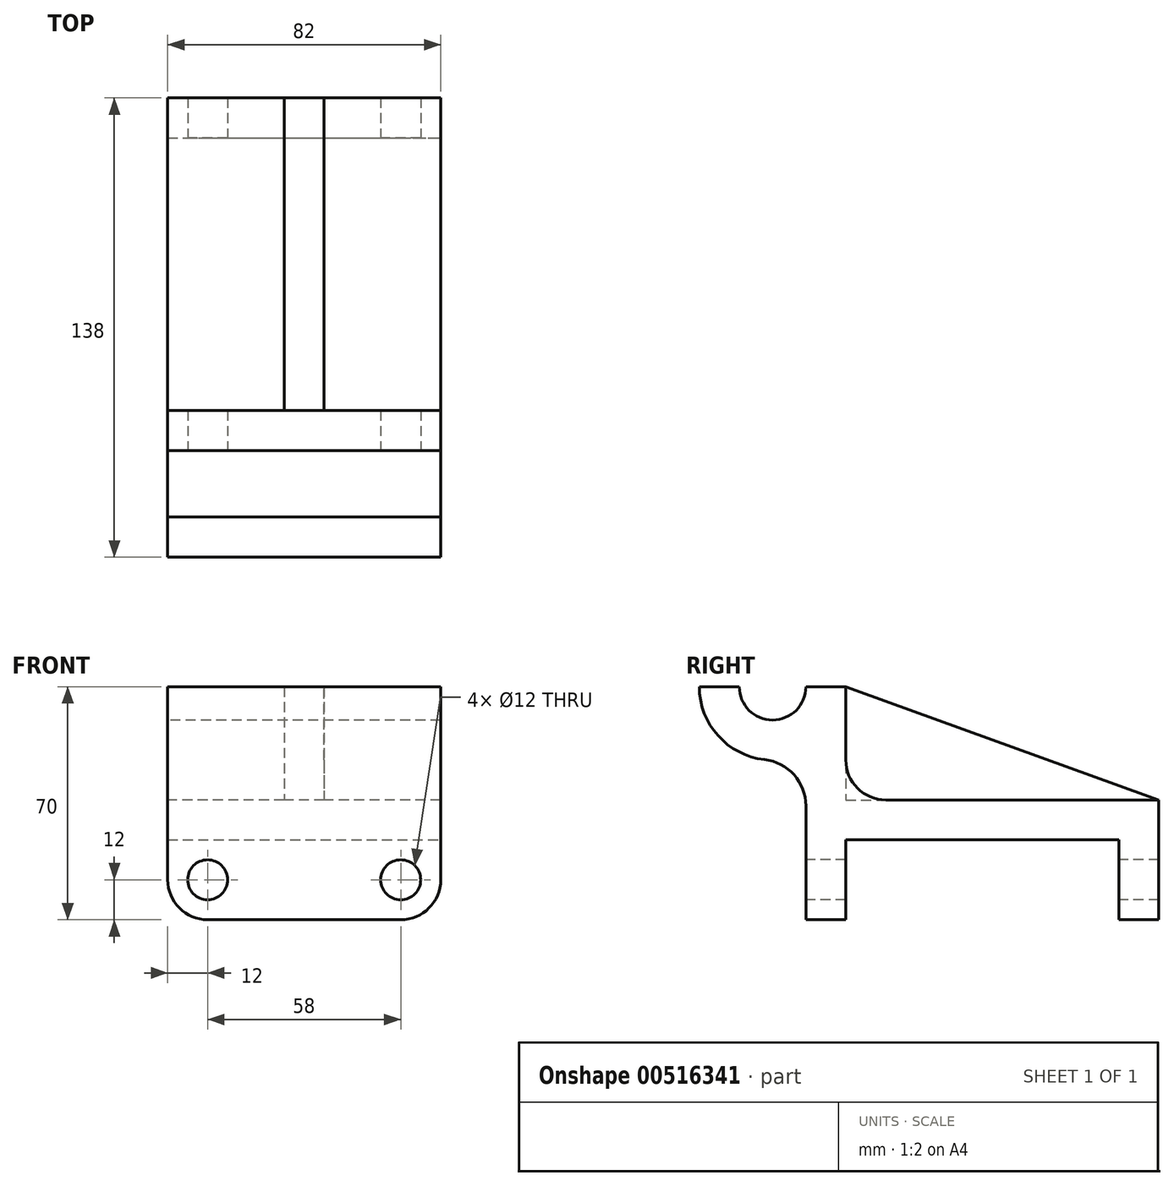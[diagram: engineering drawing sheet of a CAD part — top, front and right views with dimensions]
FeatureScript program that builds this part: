
annotation { "Feature Type Name" : "Feature", "Feature Type Description" : "" }
export const myFeature = defineFeature(function(context is Context, id is Id, definition is map)
    precondition{}
    {
        {
            var Q0;
            Q0=qCreatedBy(makeId("Top.planeOp"),FACE);
            var sketch = newSketch(context, id + "F0", { "sketchPlane" : qUnion([Q0])});
            skLineSegment(sketch, "E0.bottom", {"start": v(41, 53) * mm, "end": v(-41, 53) * mm});
            skLineSegment(sketch, "E0.top", {"start": v(41, -53) * mm, "end": v(-41, -53) * mm});
            skLineSegment(sketch, "E0.left", {"start": v(41, 53) * mm, "end": v(41, -53) * mm});
            skLineSegment(sketch, "E0.right", {"start": v(-41, 53) * mm, "end": v(-41, -53) * mm});
            skPoint(sketch, "E0.middle", {"position": v(0, 0) * mm});
            skSolve(sketch);
        }
        {
            var Q0;
            Q0 = qSketchRegion(id + "F0", true);
            extrude(context, id + "F1", {"entities" : qUnion([Q0]), "depth" : 36 * mm, "offsetDistance" : 25 * mm});
        }
        {
            var Q0;
            Q0=makeQuery(id+"F1.opExtrude","SWEPT_FACE",FACE,{"disambiguationData":[OSD([sQuery(id+"F0.wireOp",EDGE,"E0.top")])]});
            var sketch = newSketch(context, id + "F2", { "sketchPlane" : qUnion([Q0])});
            skLineSegment(sketch, "E1", {"start": v(41, 0) * mm, "end": v(29, 0) * mm});
            skLineSegment(sketch, "E2", {"start": v(29, 0) * mm, "end": v(-41, 0) * mm});
            skLineSegment(sketch, "E3", {"start": v(-41, 0) * mm, "end": v(-29, 0) * mm});
            skLineSegment(sketch, "E4", {"start": v(-29, 0) * mm, "end": v(-29, 19.34) * mm});
            skLineSegment(sketch, "E5", {"start": v(26.79, 0) * mm, "end": v(29, 0) * mm});
            skLineSegment(sketch, "E6", {"start": v(29, 0) * mm, "end": v(29, 18.35) * mm});
            skLineSegment(sketch, "E7", {"start": v(29, 0) * mm, "end": v(29, 12) * mm});
            skCircle(sketch, "E8", {"center": v(29, 12) * mm, "radius": 6 * mm});
            skLineSegment(sketch, "E9", {"start": v(-29, 0) * mm, "end": v(-29, 12) * mm});
            skCircle(sketch, "E10", {"center": v(-29, 12) * mm, "radius": 6 * mm});
            skSolve(sketch);
        }
        {
            var Q0;
            Q0=makeQuery(id+"F1.opExtrude","CAP_EDGE",EDGE,{"disambiguationData":[OSD([sQuery(id+"F0.wireOp",EDGE,"E0.right")])],"isStart":true});
            fillet(context, id + "F3", {"entities" : qUnion([Q0]), "radius" : 12 * mm, "tangentPropagation" : true, "allowEdgeOverflow" : false});
        }
        {
            var Q0;
            {var subQ0=sQuery(id+"F2.wireOp",EDGE,"E9");var subQ1=sQuery(id+"F2.wireOp",EDGE,"E4");var subQ2=makeQuery(id+"F2.imprint","INTERSECT",VERTEX,{"derivedFrom":[subQ1,subQ0]});Q0=makeQuery(id+"F2.imprint","IMPRINT",FACE,{"disambiguationData":[TD([[makeQuery(id+"F2.imprint","IMPRINT",EDGE,{"disambiguationData":[TD([[subQ2,-1.0]])],"derivedFrom":subQ1}),1.0]])]});}
            var Q1;
            {var subQ0=sQuery(id+"F2.wireOp",EDGE,"E9");var subQ1=sQuery(id+"F2.wireOp",EDGE,"E4");var subQ2=makeQuery(id+"F2.imprint","INTERSECT",VERTEX,{"derivedFrom":[subQ1,subQ0]});Q1=makeQuery(id+"F2.imprint","IMPRINT",FACE,{"disambiguationData":[TD([[makeQuery(id+"F2.imprint","IMPRINT",EDGE,{"disambiguationData":[TD([[subQ2,-1.0]])],"derivedFrom":subQ1}),-1.0]])]});}
            var Q2;
            {var subQ0=sQuery(id+"F2.wireOp",EDGE,"E7");var subQ1=sQuery(id+"F2.wireOp",EDGE,"E6");var subQ2=makeQuery(id+"F2.imprint","INTERSECT",VERTEX,{"derivedFrom":[subQ1,subQ0]});Q2=makeQuery(id+"F2.imprint","IMPRINT",FACE,{"disambiguationData":[TD([[makeQuery(id+"F2.imprint","IMPRINT",EDGE,{"disambiguationData":[TD([[subQ2,-1.0]])],"derivedFrom":subQ1}),-1.0]])]});}
            var Q3;
            {var subQ0=sQuery(id+"F2.wireOp",EDGE,"E7");var subQ1=sQuery(id+"F2.wireOp",EDGE,"E6");var subQ2=makeQuery(id+"F2.imprint","INTERSECT",VERTEX,{"derivedFrom":[subQ1,subQ0]});Q3=makeQuery(id+"F2.imprint","IMPRINT",FACE,{"disambiguationData":[TD([[makeQuery(id+"F2.imprint","IMPRINT",EDGE,{"disambiguationData":[TD([[subQ2,-1.0]])],"derivedFrom":subQ1}),1.0]])]});}
            extrude(context, id + "F4", {"entities" : qUnion([Q0, Q1, Q2, Q3]), "operationType" : NewBodyOperationType.REMOVE, "oppositeDirection" : true, "depth" : 191.1 * mm, "offsetDistance" : 25 * mm});
        }
        {
            var Q0;
            Q0=makeQuery(id+"F1.opExtrude","CAP_EDGE",EDGE,{"disambiguationData":[OSD([sQuery(id+"F0.wireOp",EDGE,"E0.left")])],"isStart":true});
            fillet(context, id + "F5", {"entities" : qUnion([Q0]), "radius" : 12 * mm, "tangentPropagation" : true, "allowEdgeOverflow" : false});
        }
        {
            var Q0;
            Q0=makeQuery(id+"F1.opExtrude","SWEPT_FACE",FACE,{"disambiguationData":[OSD([sQuery(id+"F0.wireOp",EDGE,"E0.left")])]});
            var sketch = newSketch(context, id + "F6", { "sketchPlane" : qUnion([Q0])});
            skLineSegment(sketch, "E11", {"start": v(-30.1, 36) * mm, "end": v(-30.1, 24) * mm});
            skLineSegment(sketch, "E12", {"start": v(-53, 12) * mm, "end": v(-41, 12) * mm});
            skLineSegment(sketch, "E13", {"start": v(-41, 12) * mm, "end": v(-41, 24) * mm});
            skLineSegment(sketch, "E14", {"start": v(-41, 24) * mm, "end": v(-30.1, 24) * mm});
            skLineSegment(sketch, "E15", {"start": v(53, 12) * mm, "end": v(41, 12) * mm});
            skLineSegment(sketch, "E16", {"start": v(-30.1, 24) * mm, "end": v(41, 24) * mm});
            skLineSegment(sketch, "E17", {"start": v(41, 24) * mm, "end": v(41, 12) * mm});
            skLineSegment(sketch, "E18", {"start": v(-41, 12) * mm, "end": v(-41, 0) * mm});
            skLineSegment(sketch, "E19", {"start": v(41, 12) * mm, "end": v(41, -1.92) * mm});
            skSolve(sketch);
        }
        {
            var Q0;
            {var subQ1=sQuery(id+"F6.wireOp",EDGE,"E13");Q0=makeQuery(id+"F6.imprint","IMPRINT",FACE,{"disambiguationData":[TD([[makeQuery(id+"F6.imprint","IMPRINT",EDGE,{"derivedFrom":subQ1}),-1.0]])]});}
            extrude(context, id + "F7", {"entities" : qUnion([Q0]), "operationType" : NewBodyOperationType.REMOVE, "oppositeDirection" : true, "depth" : 174.6 * mm, "offsetDistance" : 25 * mm});
        }
        {
            var Q0;
            Q0=makeQuery(id+"F7.boolean.opBoolean","COPY",FACE,{"disambiguationData":[TD([makeQuery(id+"F4.boolean.opBoolean","COPY",FACE,{"derivedFrom":makeQuery(id+"F4.opExtrude","SWEPT_FACE",FACE,{"disambiguationData":[OSD([sQuery(id+"F2.wireOp",EDGE,"E8")])]})}),makeQuery(id+"F4.boolean.opBoolean","COPY",FACE,{"derivedFrom":makeQuery(id+"F4.opExtrude","SWEPT_FACE",FACE,{"disambiguationData":[OSD([sQuery(id+"F2.wireOp",EDGE,"E10")])]})}),makeQuery(id+"F7.opExtrude","SWEPT_FACE",FACE,{"disambiguationData":[OSD([sQuery(id+"F6.wireOp",EDGE,"E13")])]}),makeQuery(id+"F7.opExtrude","SWEPT_FACE",FACE,{"disambiguationData":[OSD([sQuery(id+"F6.wireOp",EDGE,"E17")])]})])],"derivedFrom":makeQuery(id+"F7.opExtrude","SWEPT_FACE",FACE,{"disambiguationData":[OSD([sQuery(id+"F0.wireOp",EDGE,"E0.left")])]})});
            extrude(context, id + "F8", {"entities" : qUnion([Q0]), "operationType" : NewBodyOperationType.REMOVE, "oppositeDirection" : true, "depth" : 24 * mm, "offsetDistance" : 25 * mm});
        }
        {
            var Q0;
            {var subQ0=sQuery(id+"F6.wireOp",EDGE,"E11");Q0=makeQuery(id+"F6.imprint","IMPRINT",FACE,{"disambiguationData":[TD([[makeQuery(id+"F6.imprint","IMPRINT",EDGE,{"derivedFrom":subQ0}),-1.0]])]});}
            var sketch = newSketch(context, id + "F9", { "sketchPlane" : qUnion([Q0])});
            skLineSegment(sketch, "E20.0", {"start": v(-41, 12) * mm, "end": v(-41, 24) * mm});
            skLineSegment(sketch, "E21", {"start": v(-41, 12) * mm, "end": v(-41, -6.95) * mm});
            skLineSegment(sketch, "E22.0", {"start": v(41, 24) * mm, "end": v(41, 12) * mm});
            skLineSegment(sketch, "E23", {"start": v(41, 12) * mm, "end": v(41, -13.93) * mm});
            skLineSegment(sketch, "E24.bottom", {"start": v(-41, 12) * mm, "end": v(41, 12) * mm});
            skLineSegment(sketch, "E24.top", {"start": v(-41, -0.96) * mm, "end": v(41, -0.96) * mm});
            skLineSegment(sketch, "E24.left", {"start": v(-41, 12) * mm, "end": v(-41, -0.96) * mm});
            skLineSegment(sketch, "E24.right", {"start": v(41, 12) * mm, "end": v(41, -0.96) * mm});
            skSolve(sketch);
        }
        {
            var Q0;
            Q0=makeQuery(id+"F9.imprint","IMPRINT",FACE,{"disambiguationData":[TD([[makeQuery(id+"F9.imprint","IMPRINT",EDGE,{"derivedFrom":sQuery(id+"F9.wireOp",EDGE,"E24.bottom")}),-1.0]])]});
            extrude(context, id + "F10", {"entities" : qUnion([Q0]), "operationType" : NewBodyOperationType.REMOVE, "oppositeDirection" : true, "depth" : 116.9 * mm, "offsetDistance" : 25 * mm});
        }
        {
            var Q0;
            Q0=makeQuery(id+"F1.opExtrude","CAP_FACE",FACE,{"disambiguationData":[OSD([sQuery(id+"F0.wireOp",EDGE,"E0.bottom"),sQuery(id+"F0.wireOp",EDGE,"E0.top"),sQuery(id+"F0.wireOp",EDGE,"E0.left"),sQuery(id+"F0.wireOp",EDGE,"E0.right")])],"isStart":false});
            var sketch = newSketch(context, id + "F11", { "sketchPlane" : qUnion([Q0])});
            skLineSegment(sketch, "E25", {"start": v(-41, 53) * mm, "end": v(41, 53) * mm});
            skLineSegment(sketch, "E26", {"start": v(41, 53) * mm, "end": v(0, 53) * mm});
            skLineSegment(sketch, "E27", {"start": v(0, 53) * mm, "end": v(-6, 53) * mm});
            skLineSegment(sketch, "E28", {"start": v(-6, 53) * mm, "end": v(6, 53) * mm});
            skLineSegment(sketch, "E29", {"start": v(6, 53) * mm, "end": v(6, -53) * mm});
            skLineSegment(sketch, "E30", {"start": v(6, -53) * mm, "end": v(-6, -53) * mm});
            skLineSegment(sketch, "E31", {"start": v(-6, -53) * mm, "end": v(-6, 53) * mm});
            skSolve(sketch);
        }
        {
            var Q0;
            Q0 = qSketchRegion(id + "F11", true);
            extrude(context, id + "F12", {"entities" : qUnion([Q0]), "operationType" : NewBodyOperationType.ADD, "depth" : 34 * mm, "offsetDistance" : 25 * mm});
        }
        {
            var Q0;
            Q0=makeQuery(id+"F12.opExtrude","SWEPT_FACE",FACE,{"disambiguationData":[OSD([sQuery(id+"F11.wireOp",EDGE,"E31")])]});
            var sketch = newSketch(context, id + "F13", { "sketchPlane" : qUnion([Q0])});
            skLineSegment(sketch, "E32.0", {"start": v(41, 12) * mm, "end": v(41, 24) * mm});
            skLineSegment(sketch, "E33", {"start": v(-53, 36) * mm, "end": v(41, 70) * mm});
            skSolve(sketch);
        }
        {
            var Q0;
            {var subQ0=sQuery(id+"F13.wireOp",EDGE,"E33");Q0=makeQuery(id+"F13.imprint","IMPRINT",FACE,{"disambiguationData":[TD([[makeQuery(id+"F13.imprint","IMPRINT",EDGE,{"derivedFrom":subQ0}),1.0]])]});}
            extrude(context, id + "F14", {"entities" : qUnion([Q0]), "operationType" : NewBodyOperationType.REMOVE, "oppositeDirection" : true, "depth" : 25 * mm, "offsetDistance" : 25 * mm});
        }
        {
            var Q0;
            Q0=makeQuery(id+"F12.opExtrude","SWEPT_FACE",FACE,{"disambiguationData":[OSD([sQuery(id+"F11.wireOp",EDGE,"E31")])]});
            var sketch = newSketch(context, id + "F15", { "sketchPlane" : qUnion([Q0])});
            skLineSegment(sketch, "E34", {"start": v(41, 70) * mm, "end": v(41, 36) * mm});
            skSolve(sketch);
        }
        {
            var Q0;
            {var subQ0=sQuery(id+"F15.wireOp",EDGE,"E34");Q0=makeQuery(id+"F15.imprint","IMPRINT",FACE,{"disambiguationData":[TD([[makeQuery(id+"F15.imprint","IMPRINT",EDGE,{"derivedFrom":subQ0}),1.0]])]});}
            extrude(context, id + "F16", {"entities" : qUnion([Q0]), "operationType" : NewBodyOperationType.REMOVE, "oppositeDirection" : true, "depth" : 25 * mm, "offsetDistance" : 25 * mm});
        }
        {
            var Q0;
            {var subQ0=sQuery(id+"F11.wireOp",EDGE,"E31");var subQ1=makeQuery(id+"F12.opExtrude","CAP_EDGE",EDGE,{"disambiguationData":[OSD([subQ0])],"isStart":true});var subQ3=sQuery(id+"F0.wireOp",EDGE,"E0.top");var subQ6=sQuery(id+"F0.wireOp",EDGE,"E0.right");var subQ7=sQuery(id+"F0.wireOp",EDGE,"E0.bottom");var subQ10=sQuery(id+"F0.wireOp",EDGE,"E0.left");var subQ11=makeQuery(id+"F1.opExtrude","CAP_FACE",FACE,{"disambiguationData":[OSD([subQ7,subQ3,subQ10,subQ6])],"isStart":false});Q0=makeQuery(id+"F16.boolean.opBoolean","MERGE",FACE,{"derivedFrom":[makeQuery(id+"F12.boolean.opBoolean","SPLIT",FACE,{"disambiguationData":[TD([makeQuery(id+"F1.opExtrude","SWEPT_FACE",FACE,{"disambiguationData":[OSD([subQ10])]})])],"derivedFrom":subQ11}),makeQuery(id+"F12.boolean.opBoolean","SPLIT",FACE,{"disambiguationData":[TD([makeQuery(id+"F1.opExtrude","SWEPT_FACE",FACE,{"disambiguationData":[OSD([subQ6])]})])],"derivedFrom":subQ11}),makeQuery(id+"F16.opExtrude","SWEPT_FACE",FACE,{"disambiguationData":[OSD([subQ0]),TDD([makeQuery(id+"F15.imprint","IMPRINT",EDGE,{"disambiguationData":[TD([[makeQuery(id+"F15.imprint","INTERSECT",VERTEX,{"derivedFrom":[subQ1,sQuery(id+"F15.wireOp",EDGE,"E34")]}),1.0]])],"derivedFrom":subQ1})])]})]});}
            var sketch = newSketch(context, id + "F17", { "sketchPlane" : qUnion([Q0])});
            skLineSegment(sketch, "E35", {"start": v(41, -41) * mm, "end": v(-41, -41) * mm});
            skSolve(sketch);
        }
        {
            var Q0;
            {var subQ0=sQuery(id+"F17.wireOp",EDGE,"E35");var subQ1=sQuery(id+"F11.wireOp",EDGE,"E29");var subQ2=makeQuery(id+"F17.imprint","INTERSECT",VERTEX,{"derivedFrom":[makeQuery(id+"F12.opExtrude","CAP_EDGE",EDGE,{"disambiguationData":[OSD([subQ1])],"isStart":true}),subQ0]});Q0=makeQuery(id+"F17.imprint","IMPRINT",FACE,{"disambiguationData":[TD([[makeQuery(id+"F17.imprint","IMPRINT",EDGE,{"disambiguationData":[TD([[subQ2,1.0]])],"derivedFrom":subQ0}),1.0]])]});}
            extrude(context, id + "F18", {"entities" : qUnion([Q0]), "operationType" : NewBodyOperationType.ADD, "depth" : 34 * mm, "offsetDistance" : 25 * mm});
        }
        {
            var Q0;
            {var subQ3=sQuery(id+"F17.wireOp",EDGE,"E35");var subQ4=sQuery(id+"F0.wireOp",EDGE,"E0.right");Q0=makeQuery(id+"F18.boolean.opBoolean","SPLIT",EDGE,{"disambiguationData":[TD([makeQuery(id+"F1.opExtrude","SWEPT_FACE",FACE,{"disambiguationData":[OSD([subQ4])]})])],"derivedFrom":makeQuery(id+"F18.opExtrude","CAP_EDGE",EDGE,{"disambiguationData":[OSD([subQ3])],"isStart":true})});}
            var Q1;
            {var subQ3=sQuery(id+"F17.wireOp",EDGE,"E35");var subQ4=sQuery(id+"F0.wireOp",EDGE,"E0.left");Q1=makeQuery(id+"F18.boolean.opBoolean","SPLIT",EDGE,{"disambiguationData":[TD([makeQuery(id+"F1.opExtrude","SWEPT_FACE",FACE,{"disambiguationData":[OSD([subQ4])]})])],"derivedFrom":makeQuery(id+"F18.opExtrude","CAP_EDGE",EDGE,{"disambiguationData":[OSD([subQ3])],"isStart":true})});}
            fillet(context, id + "F19", {"entities" : qUnion([Q0, Q1]), "radius" : 12 * mm, "tangentPropagation" : true, "allowEdgeOverflow" : false});
        }
        {
            var Q0;
            {var subQ0=sQuery(id+"F0.wireOp",EDGE,"E0.right");Q0=makeQuery(id+"F18.boolean.opBoolean","MERGE",FACE,{"derivedFrom":[makeQuery(id+"F1.opExtrude","SWEPT_FACE",FACE,{"disambiguationData":[OSD([subQ0])]}),makeQuery(id+"F18.opExtrude","SWEPT_FACE",FACE,{"disambiguationData":[OSD([subQ0])]})]});}
            var sketch = newSketch(context, id + "F20", { "sketchPlane" : qUnion([Q0])});
            skArc(sketch, "E36", {"start": v(41, 70) * mm, "mid": v(63, 48) * mm, "end": v(85, 70) * mm});
            skCircle(sketch, "E37", {"center": v(63, 70) * mm, "radius": 10 * mm});
            skLineSegment(sketch, "E38", {"start": v(41, 70) * mm, "end": v(85, 70) * mm});
            skSolve(sketch);
        }
        {
            var Q0;
            {var subQ0=sQuery(id+"F20.wireOp",EDGE,"E38");var subQ1=sQuery(id+"F20.wireOp",EDGE,"E36");var subQ2=makeQuery(id+"F20.imprint","INTERSECT",VERTEX,{"derivedFrom":[subQ1,subQ0]});Q0=makeQuery(id+"F20.imprint","IMPRINT",FACE,{"disambiguationData":[TD([[makeQuery(id+"F20.imprint","IMPRINT",EDGE,{"disambiguationData":[TD([[subQ2,1.0]])],"derivedFrom":subQ0}),-1.0]])]});}
            var Q1;
            {var subQ0=sQuery(id+"F20.wireOp",EDGE,"E38");var subQ1=sQuery(id+"F20.wireOp",EDGE,"E36");var subQ2=sQuery(id+"F0.wireOp",EDGE,"E0.right");var subQ3=makeQuery(id+"F20.imprint","INTERSECT",VERTEX,{"derivedFrom":[makeQuery(id+"F18.opExtrude","SWEPT_EDGE",EDGE,{"disambiguationData":[OSD([subQ2,sQuery(id+"F17.wireOp",EDGE,"E35")])]}),subQ1,subQ0]});Q1=makeQuery(id+"F20.imprint","IMPRINT",FACE,{"disambiguationData":[TD([[makeQuery(id+"F20.imprint","IMPRINT",EDGE,{"disambiguationData":[TD([[subQ3,-1.0]])],"derivedFrom":subQ1}),1.0]])]});}
            var Q2;
            {var subQ0=sQuery(id+"F0.wireOp",EDGE,"E0.left");Q2=makeQuery(id+"F18.boolean.opBoolean","MERGE",FACE,{"derivedFrom":[makeQuery(id+"F1.opExtrude","SWEPT_FACE",FACE,{"disambiguationData":[OSD([subQ0])]}),makeQuery(id+"F18.opExtrude","SWEPT_FACE",FACE,{"disambiguationData":[OSD([subQ0])]})]});}
            extrude(context, id + "F21", {"entities" : qUnion([Q0, Q1]), "operationType" : NewBodyOperationType.ADD, "endBound" : BoundingType.UP_TO_SURFACE, "oppositeDirection" : true, "depth" : 86 * mm, "endBoundEntityFace" : qUnion([Q2]), "offsetDistance" : 25 * mm});
        }
        {
            var Q0;
            {var subQ0=sQuery(id+"F11.wireOp",EDGE,"E30");var subQ1=sQuery(id+"F0.wireOp",EDGE,"E0.top");Q0=makeQuery(id+"F21.boolean.opBoolean","INTERSECT",EDGE,{"derivedFrom":[makeQuery(id+"F18.boolean.opBoolean","MERGE",FACE,{"derivedFrom":[makeQuery(id+"F12.boolean.opBoolean","MERGE",FACE,{"derivedFrom":[makeQuery(id+"F1.opExtrude","SWEPT_FACE",FACE,{"disambiguationData":[OSD([subQ1])]}),makeQuery(id+"F12.opExtrude","SWEPT_FACE",FACE,{"disambiguationData":[OSD([subQ0])]})]}),makeQuery(id+"F18.opExtrude","SWEPT_FACE",FACE,{"disambiguationData":[OSD([subQ1,subQ0,sQuery(id+"F11.wireOp",EDGE,"E31")])]})]}),makeQuery(id+"F21.opExtrude","SWEPT_FACE",FACE,{"disambiguationData":[OSD([sQuery(id+"F20.wireOp",EDGE,"E36")])]})]});}
            fillet(context, id + "F22", {"entities" : qUnion([Q0]), "radius" : 14 * mm, "tangentPropagation" : true, "allowEdgeOverflow" : false});
        }
    });
